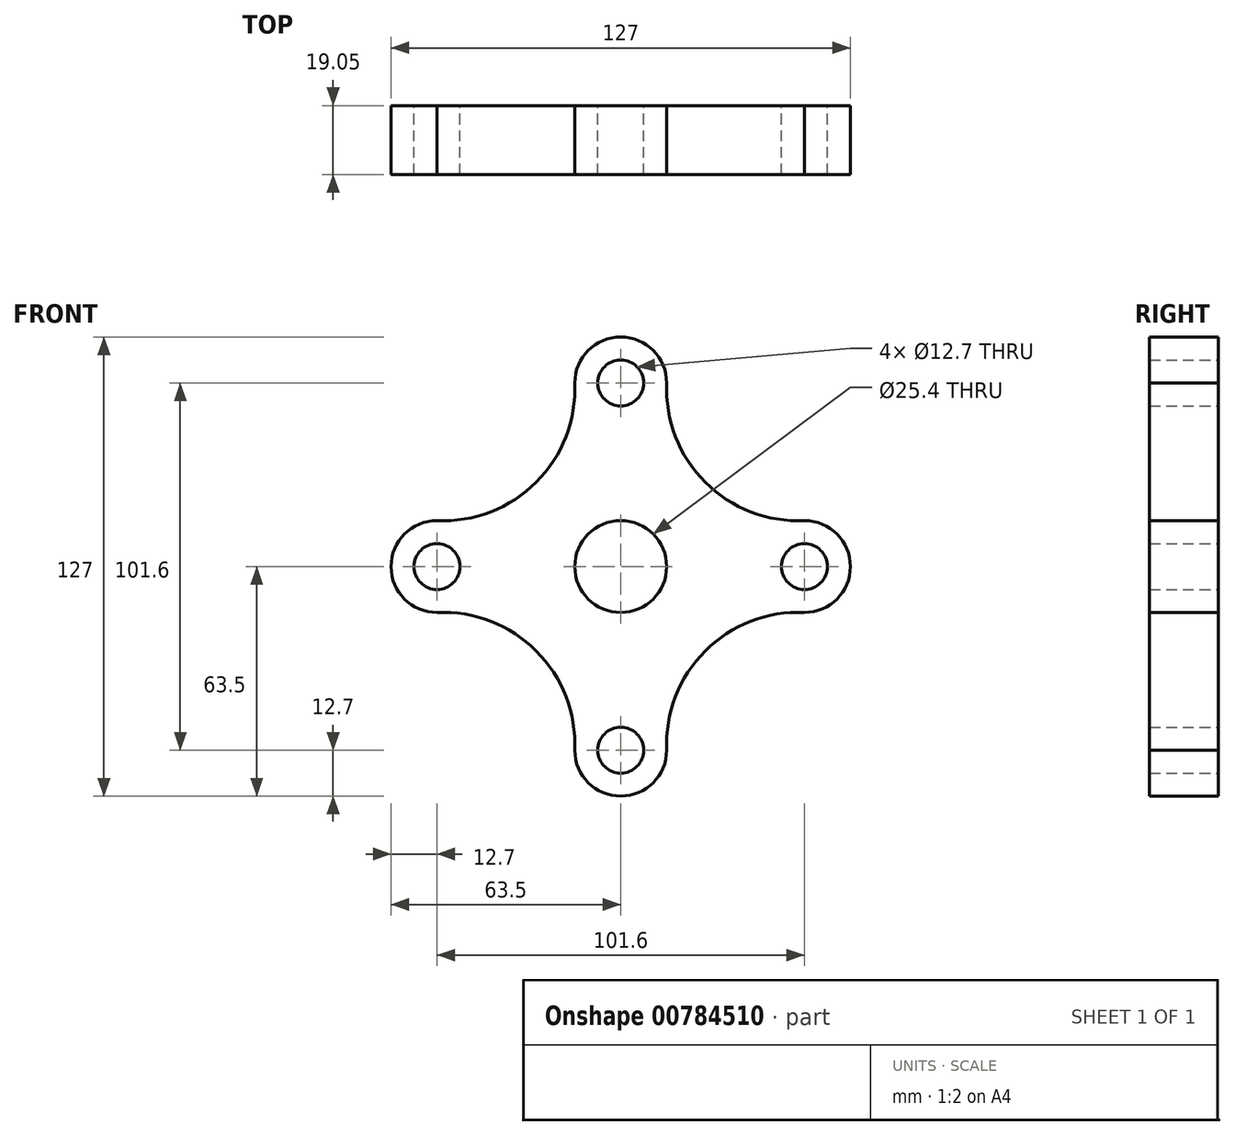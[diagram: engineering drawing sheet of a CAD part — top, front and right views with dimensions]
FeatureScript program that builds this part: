
annotation { "Feature Type Name" : "Feature", "Feature Type Description" : "" }
export const myFeature = defineFeature(function(context is Context, id is Id, definition is map)
    precondition{}
    {
        {
            var Q0;
            Q0=qCreatedBy(makeId("Front.planeOp"),FACE);
            var sketch = newSketch(context, id + "F0", { "sketchPlane" : qUnion([Q0])});
            skLineSegment(sketch, "E0", {"start": v(0, -12.7) * mm, "end": v(0, -50.8) * mm});
            skCircle(sketch, "E1", {"center": v(0, 0) * mm, "radius": 12.7 * mm});
            skLineSegment(sketch, "E2", {"start": v(-12.7, 0) * mm, "end": v(-44.45, 0) * mm});
            skCircle(sketch, "E3", {"center": v(-50.8, 0) * mm, "radius": 6.35 * mm});
            skCircle(sketch, "E4", {"center": v(50.8, 0) * mm, "radius": 6.35 * mm});
            skCircle(sketch, "E5", {"center": v(0, -50.8) * mm, "radius": 6.35 * mm});
            skCircle(sketch, "E6", {"center": v(0, 50.8) * mm, "radius": 6.35 * mm});
            skArc(sketch, "E7", {"start": v(-50.8, 12.7) * mm, "mid": v(-63.5, 0) * mm, "end": v(-50.8, -12.7) * mm});
            skArc(sketch, "E8", {"start": v(12.7, 50.8) * mm, "mid": v(0, 63.5) * mm, "end": v(-12.7, 50.8) * mm});
            skArc(sketch, "E9", {"start": v(50.8, -12.7) * mm, "mid": v(63.5, 0) * mm, "end": v(50.8, 12.7) * mm});
            skArc(sketch, "E10", {"start": v(-12.7, -50.8) * mm, "mid": v(0, -63.5) * mm, "end": v(12.7, -50.8) * mm});
            skArc(sketch, "E11", {"start": v(-50.8, 12.7) * mm, "mid": v(-23.36, 23.36) * mm, "end": v(-12.7, 50.8) * mm});
            skArc(sketch, "E12", {"start": v(12.7, 50.8) * mm, "mid": v(23.36, 23.36) * mm, "end": v(50.8, 12.7) * mm});
            skArc(sketch, "E13", {"start": v(50.8, -12.7) * mm, "mid": v(23.36, -23.36) * mm, "end": v(12.7, -50.8) * mm});
            skArc(sketch, "E14", {"start": v(-12.7, -50.8) * mm, "mid": v(-23.36, -23.36) * mm, "end": v(-50.8, -12.7) * mm});
            skSolve(sketch);
        }
        {
            var Q0;
            Q0 = qSketchRegion(id + "F0", true);
            extrude(context, id + "F1", {"entities" : qUnion([Q0]), "depth" : 19.05 * mm, "offsetDistance" : 25.4 * mm});
        }
    });
